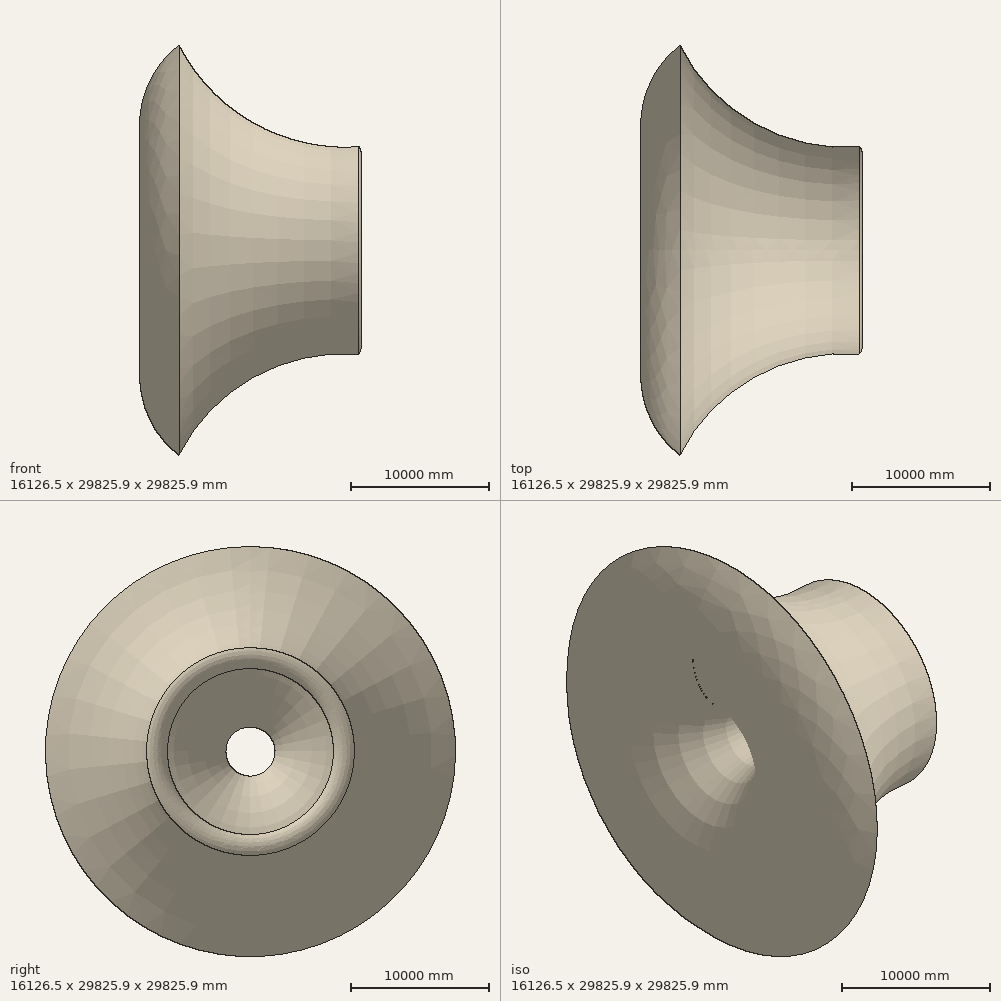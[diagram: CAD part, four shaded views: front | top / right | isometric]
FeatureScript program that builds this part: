
annotation { "Feature Type Name" : "Feature", "Feature Type Description" : "" }
export const myFeature = defineFeature(function(context is Context, id is Id, definition is map)
    precondition{}
    {
        {
            var Q0;
            Q0=qCreatedBy(makeId("Front.planeOp"),FACE);
            var sketch = newSketch(context, id + "F0", { "sketchPlane" : qUnion([Q0])});
            skArc(sketch, "E0", {"start": v(10884.51, 14912.91) * mm, "mid": v(11058.95, 3156.11) * mm, "end": v(22258.73, 6736.27) * mm});
            skArc(sketch, "E1", {"start": v(22258.73, 6736.27) * mm, "mid": v(23600.29, 6126.83) * mm, "end": v(23948.88, 7558.5) * mm});
            skArc(sketch, "E2", {"start": v(10884.51, 14912.91) * mm, "mid": v(16308.65, 9267.38) * mm, "end": v(23948.88, 7558.5) * mm});
            skSolve(sketch);
        }
        {
            var Q0;
            Q0=qCreatedBy(makeId("Front.planeOp"),FACE);
            var sketch = newSketch(context, id + "F1", { "sketchPlane" : qUnion([Q0])});
            skLineSegment(sketch, "E3", {"start": v(0, 0) * mm, "end": v(26496.95, 0) * mm, "construction": true});
            skLineSegment(sketch, "E4", {"start": v(0, 0) * mm, "end": v(25399.93, 57.63) * mm});
            skLineSegment(sketch, "E5", {"start": v(25399.93, 57.63) * mm, "end": v(25399.93, 0) * mm});
            skSolve(sketch);
        }
        {
            var Q0;
            Q0 = qSketchRegion(id + "F0", true);
            extrude(context, id + "F2", {"entities" : qUnion([Q0]), "depth" : 25.4 * mm, "offsetDistance" : 25.4 * mm});
        }
        {
            var Q0;
            Q0=makeQuery(id+"F2.opExtrude","CAP_FACE",FACE,{"disambiguationData":[OSD([sQuery(id+"F0.wireOp",EDGE,"E0"),sQuery(id+"F0.wireOp",EDGE,"E1"),sQuery(id+"F0.wireOp",EDGE,"E2")])],"isStart":false});
            var sketch = newSketch(context, id + "F3", { "sketchPlane" : qUnion([Q0])});
            skSolve(sketch);
        }
        {
            var Q0;
            Q0 = qSketchRegion(id + "F3", true);
            var Q1;
            Q1=makeQuery(id+"F3.imprint","IMPRINT",FACE,{"disambiguationData":[TD([[makeQuery(id+"F3.imprint","IMPRINT",EDGE,{"derivedFrom":makeQuery(id+"F2.opExtrude","CAP_EDGE",EDGE,{"disambiguationData":[OSD([sQuery(id+"F0.wireOp",EDGE,"E0")])],"isStart":false})}),1.0]])]});
            var Q2;
            Q2=sQuery(id+"F1.wireOp",EDGE,"E3");
            revolve(context, id + "F4", {"operationType" : NewBodyOperationType.ADD, "surfaceOperationType" : NewSurfaceOperationType.NEW, "entities" : qUnion([Q0, Q1]), "axis" : qUnion([Q2]), "revolveType" : RevolveType.FULL});
        }
    });
